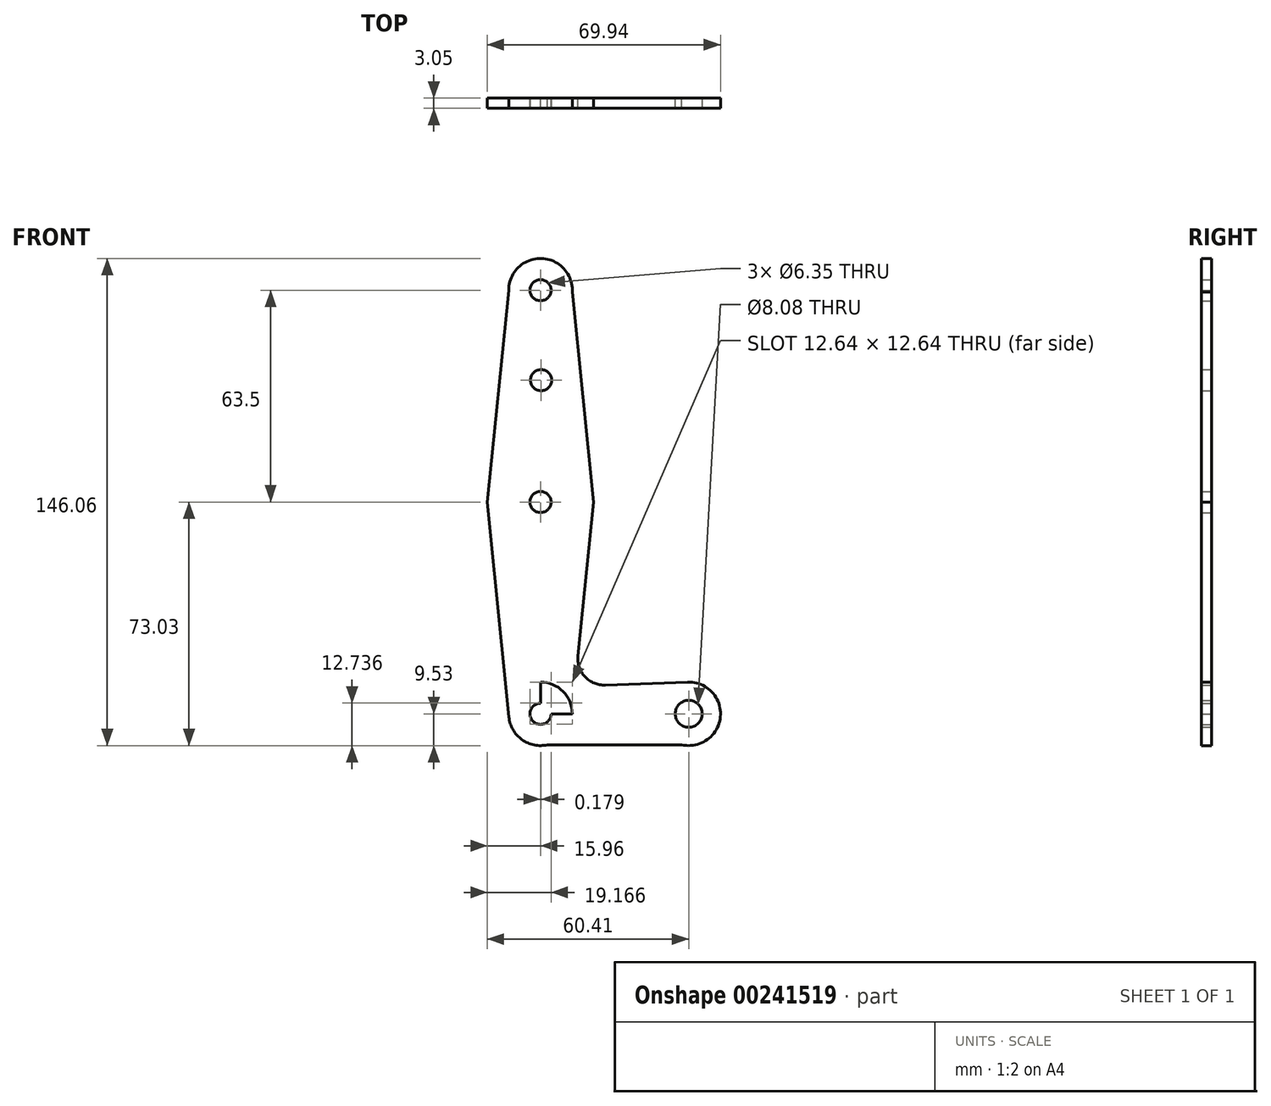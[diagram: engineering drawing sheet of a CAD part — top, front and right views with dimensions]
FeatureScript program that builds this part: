
annotation { "Feature Type Name" : "Feature", "Feature Type Description" : "" }
export const myFeature = defineFeature(function(context is Context, id is Id, definition is map)
    precondition{}
    {
        {
            var Q0;
            Q0=qCreatedBy(makeId("Front.planeOp"),FACE);
            var sketch = newSketch(context, id + "F0", { "sketchPlane" : qUnion([Q0])});
            skCircle(sketch, "E0", {"center": v(0, 63.5) * mm, "radius": 9.53 * mm});
            skCircle(sketch, "E1", {"center": v(0, 63.5) * mm, "radius": 3.18 * mm});
            skCircle(sketch, "E2", {"center": v(0, 0) * mm, "radius": 15.88 * mm});
            skCircle(sketch, "E3", {"center": v(0, -63.5) * mm, "radius": 9.53 * mm});
            skCircle(sketch, "E4", {"center": v(44.45, -63.5) * mm, "radius": 9.53 * mm});
            skCircle(sketch, "E5", {"center": v(0, 0) * mm, "radius": 3.18 * mm});
            skCircle(sketch, "E6", {"center": v(0, -63.5) * mm, "radius": 3.18 * mm});
            skCircle(sketch, "E7", {"center": v(44.45, -63.5) * mm, "radius": 4.04 * mm});
            skCircle(sketch, "E8", {"center": v(0.18, 36.52) * mm, "radius": 3.18 * mm});
            skLineSegment(sketch, "E9", {"start": v(0, 63.5) * mm, "end": v(0, 0) * mm});
            skLineSegment(sketch, "E10", {"start": v(0, 0) * mm, "end": v(0, -63.5) * mm});
            skLineSegment(sketch, "E11", {"start": v(0, -63.5) * mm, "end": v(40.41, -63.5) * mm});
            skLineSegment(sketch, "E12", {"start": v(40.41, -63.5) * mm, "end": v(44.45, -63.5) * mm});
            skLineSegment(sketch, "E13", {"start": v(-9.53, 63.5) * mm, "end": v(-15.96, 0) * mm});
            skLineSegment(sketch, "E14", {"start": v(-15.96, 0) * mm, "end": v(-9.48, -64.45) * mm});
            skLineSegment(sketch, "E15", {"start": v(9.5, 62.9) * mm, "end": v(15.96, 0) * mm});
            skLineSegment(sketch, "E16", {"start": v(15.96, 0) * mm, "end": v(11.23, -46.13) * mm});
            skLineSegment(sketch, "E17", {"start": v(2.11, -72.79) * mm, "end": v(46.56, -72.79) * mm});
            skLineSegment(sketch, "E18", {"start": v(19.43, -54.88) * mm, "end": v(44.1, -53.98) * mm});
            skArc(sketch, "E19.filletArc", {"start": v(11.23, -46.13) * mm, "mid": v(13.33, -52.37) * mm, "end": v(19.43, -54.88) * mm});
            skSolve(sketch);
        }
        {
            var Q0;
            Q0 = qSketchRegion(id + "F0", true);
            var Q1;
            {var subQ1=sQuery(id+"F0.wireOp",EDGE,"E0");var subQ6=sQuery(id+"F0.wireOp",EDGE,"E13");var subQ10=makeQuery(id+"F0.imprint","INTERSECT",VERTEX,{"derivedFrom":[subQ1,subQ6]});Q1=makeQuery(id+"F0.imprint","IMPRINT",FACE,{"disambiguationData":[TD([[makeQuery(id+"F0.imprint","IMPRINT",EDGE,{"disambiguationData":[TD([[subQ10,-1.0]])],"derivedFrom":subQ1}),-1.0]])]});}
            extrude(context, id + "F1", {"entities" : qUnion([Q0, Q1]), "depth" : 3.05 * mm});
        }
    });
